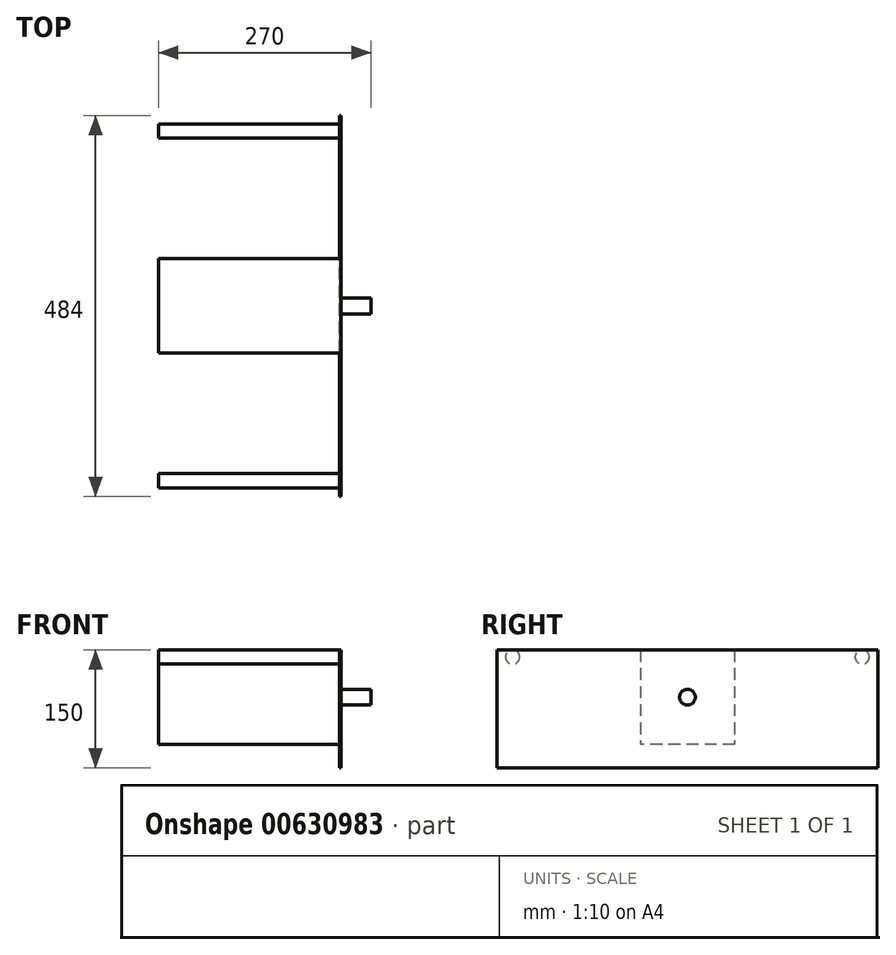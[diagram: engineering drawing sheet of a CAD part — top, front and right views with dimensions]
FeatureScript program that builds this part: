
annotation { "Feature Type Name" : "Feature", "Feature Type Description" : "" }
export const myFeature = defineFeature(function(context is Context, id is Id, definition is map)
    precondition{}
    {
        {
            var Q0;
            Q0=qCreatedBy(makeId("Top.planeOp"),FACE);
            var sketch = newSketch(context, id + "F0", { "sketchPlane" : qUnion([Q0])});
            skLineSegment(sketch, "E0.bottom", {"start": v(-58.94, 101) * mm, "end": v(171.06, 101) * mm});
            skLineSegment(sketch, "E0.top", {"start": v(-58.94, -19) * mm, "end": v(171.06, -19) * mm});
            skLineSegment(sketch, "E0.left", {"start": v(-58.94, 101) * mm, "end": v(-58.94, -19) * mm});
            skLineSegment(sketch, "E0.right", {"start": v(171.06, 101) * mm, "end": v(171.06, -19) * mm});
            skSolve(sketch);
        }
        {
            var Q0;
            Q0 = qSketchRegion(id + "F0", true);
            extrude(context, id + "F1", {"entities" : qUnion([Q0]), "depth" : 120 * mm, "offsetDistance" : 25 * mm});
        }
        {
            var Q0;
            Q0=makeQuery(id+"F1.opExtrude","SWEPT_FACE",FACE,{"disambiguationData":[OSD([sQuery(id+"F0.wireOp",EDGE,"E0.right")])]});
            var sketch = newSketch(context, id + "F2", { "sketchPlane" : qUnion([Q0])});
            skCircle(sketch, "E1", {"center": v(41, 60) * mm, "radius": 10 * mm});
            skSolve(sketch);
        }
        {
            var Q0;
            Q0 = qSketchRegion(id + "F2", true);
            extrude(context, id + "F3", {"entities" : qUnion([Q0]), "operationType" : NewBodyOperationType.ADD, "depth" : 40 * mm, "offsetDistance" : 25 * mm});
        }
        {
            var Q0;
            Q0=makeQuery(id+"F1.opExtrude","SWEPT_FACE",FACE,{"disambiguationData":[OSD([sQuery(id+"F0.wireOp",EDGE,"E0.right")])]});
            var sketch = newSketch(context, id + "F4", { "sketchPlane" : qUnion([Q0])});
            skLineSegment(sketch, "E2.bottom", {"start": v(-201, 120) * mm, "end": v(283, 120) * mm});
            skLineSegment(sketch, "E2.top", {"start": v(-201, -30) * mm, "end": v(283, -30) * mm});
            skLineSegment(sketch, "E2.left", {"start": v(-201, 120) * mm, "end": v(-201, -30) * mm});
            skLineSegment(sketch, "E2.right", {"start": v(283, 120) * mm, "end": v(283, -30) * mm});
            skSolve(sketch);
        }
        {
            var Q0;
            Q0 = qSketchRegion(id + "F4", true);
            extrude(context, id + "F5", {"entities" : qUnion([Q0]), "operationType" : NewBodyOperationType.ADD, "depth" : 2 * mm, "offsetDistance" : 25 * mm});
        }
        {
            var Q0;
            Q0=makeQuery(id+"F5.opExtrude","CAP_FACE",FACE,{"disambiguationData":[OSD([sQuery(id+"F4.wireOp",EDGE,"E2.bottom"),sQuery(id+"F4.wireOp",EDGE,"E2.top"),sQuery(id+"F4.wireOp",EDGE,"E2.left"),sQuery(id+"F4.wireOp",EDGE,"E2.right")])],"isStart":true});
            var sketch = newSketch(context, id + "F6", { "sketchPlane" : qUnion([Q0])});
            skCircle(sketch, "E3", {"center": v(-263, 111) * mm, "radius": 9 * mm});
            skCircle(sketch, "E4.1.0.0", {"center": v(181, 111) * mm, "radius": 9 * mm});
            skLineSegment(sketch, "E4.direction1", {"start": v(-263, 111) * mm, "end": v(181, 111) * mm, "construction": true});
            skSolve(sketch);
        }
        {
            var Q0;
            Q0=makeQuery(id+"F6.imprint","IMPRINT",FACE,{"disambiguationData":[TD([[makeQuery(id+"F6.imprint","IMPRINT",EDGE,{"derivedFrom":sQuery(id+"F6.wireOp",EDGE,"E4.1.0.0")}),1.0]])]});
            var Q1;
            Q1=makeQuery(id+"F6.imprint","IMPRINT",FACE,{"disambiguationData":[TD([[makeQuery(id+"F6.imprint","IMPRINT",EDGE,{"derivedFrom":sQuery(id+"F6.wireOp",EDGE,"E3")}),1.0]])]});
            var Q2;
            Q2=sQuery(id+"F6.wireOp",EDGE,"E3");
            var Q3;
            Q3=sQuery(id+"F6.wireOp",EDGE,"E4.1.0.0");
            extrude(context, id + "F7", {"entities" : qUnion([Q0, Q1]), "operationType" : NewBodyOperationType.ADD, "surfaceEntities" : qUnion([Q2, Q3]), "depth" : 230 * mm, "offsetDistance" : 25 * mm});
        }
    });
